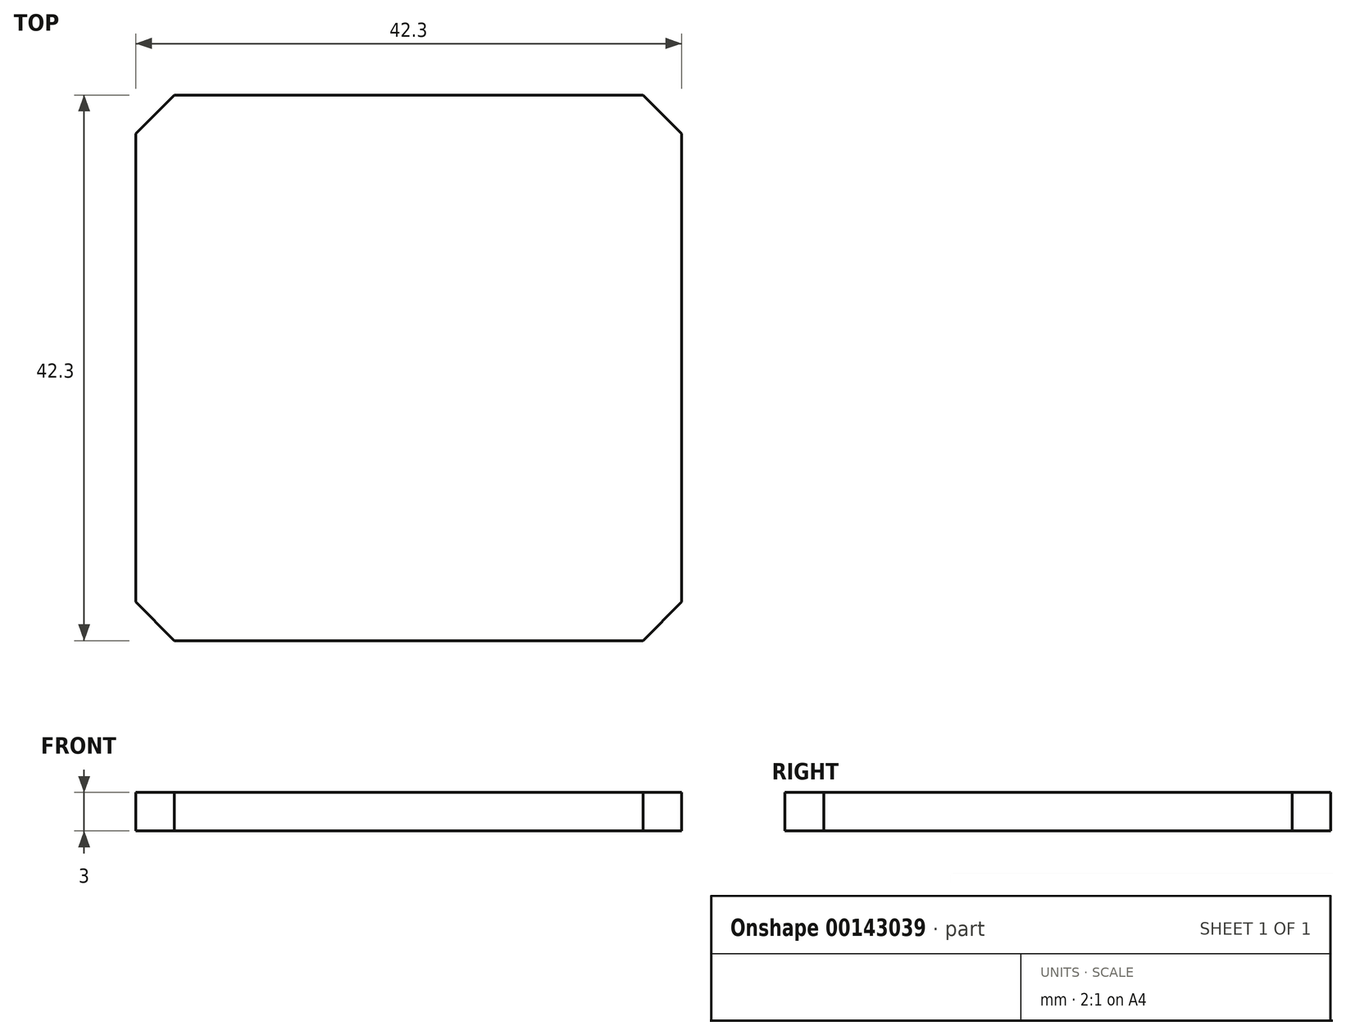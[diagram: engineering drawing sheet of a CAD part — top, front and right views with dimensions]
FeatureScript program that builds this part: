
annotation { "Feature Type Name" : "Feature", "Feature Type Description" : "" }
export const myFeature = defineFeature(function(context is Context, id is Id, definition is map)
    precondition{}
    {
        {
            var Q0;
            Q0=qCreatedBy(makeId("Top.planeOp"),FACE);
            var sketch = newSketch(context, id + "F0", { "sketchPlane" : qUnion([Q0])});
            skPoint(sketch, "E0", {"position": v(18.15, 0) * mm});
            skPoint(sketch, "E1", {"position": v(0, -18.15) * mm});
            skPoint(sketch, "E2", {"position": v(-18.15, 0) * mm});
            skLineSegment(sketch, "E3", {"start": v(0, -18.15) * mm, "end": v(18.15, -18.15) * mm});
            skLineSegment(sketch, "E4", {"start": v(18.15, -18.15) * mm, "end": v(21.15, -15.15) * mm});
            skLineSegment(sketch, "E5", {"start": v(21.15, -15.15) * mm, "end": v(21.15, 21.15) * mm});
            skLineSegment(sketch, "E6", {"start": v(21.15, 21.15) * mm, "end": v(18.15, 24.15) * mm});
            skLineSegment(sketch, "E7", {"start": v(18.15, 24.15) * mm, "end": v(0, 24.15) * mm});
            skLineSegment(sketch, "E8", {"start": v(0, 24.15) * mm, "end": v(0, -18.15) * mm, "construction": true});
            skLineSegment(sketch, "E9.MirrorCS", {"start": v(-18.15, 24.15) * mm, "end": v(0, 24.15) * mm});
            skLineSegment(sketch, "E10.MirrorCS", {"start": v(-21.15, 21.15) * mm, "end": v(-18.15, 24.15) * mm});
            skLineSegment(sketch, "E11.MirrorCS", {"start": v(-21.15, -15.15) * mm, "end": v(-21.15, 21.15) * mm});
            skLineSegment(sketch, "E12.MirrorCS", {"start": v(-18.15, -18.15) * mm, "end": v(-21.15, -15.15) * mm});
            skLineSegment(sketch, "E13.MirrorCS", {"start": v(0, -18.15) * mm, "end": v(-18.15, -18.15) * mm});
            skSolve(sketch);
        }
        {
            var Q0;
            Q0 = qSketchRegion(id + "F0", true);
            extrude(context, id + "F1", {"entities" : qUnion([Q0]), "depth" : 3 * mm});
        }
    });
